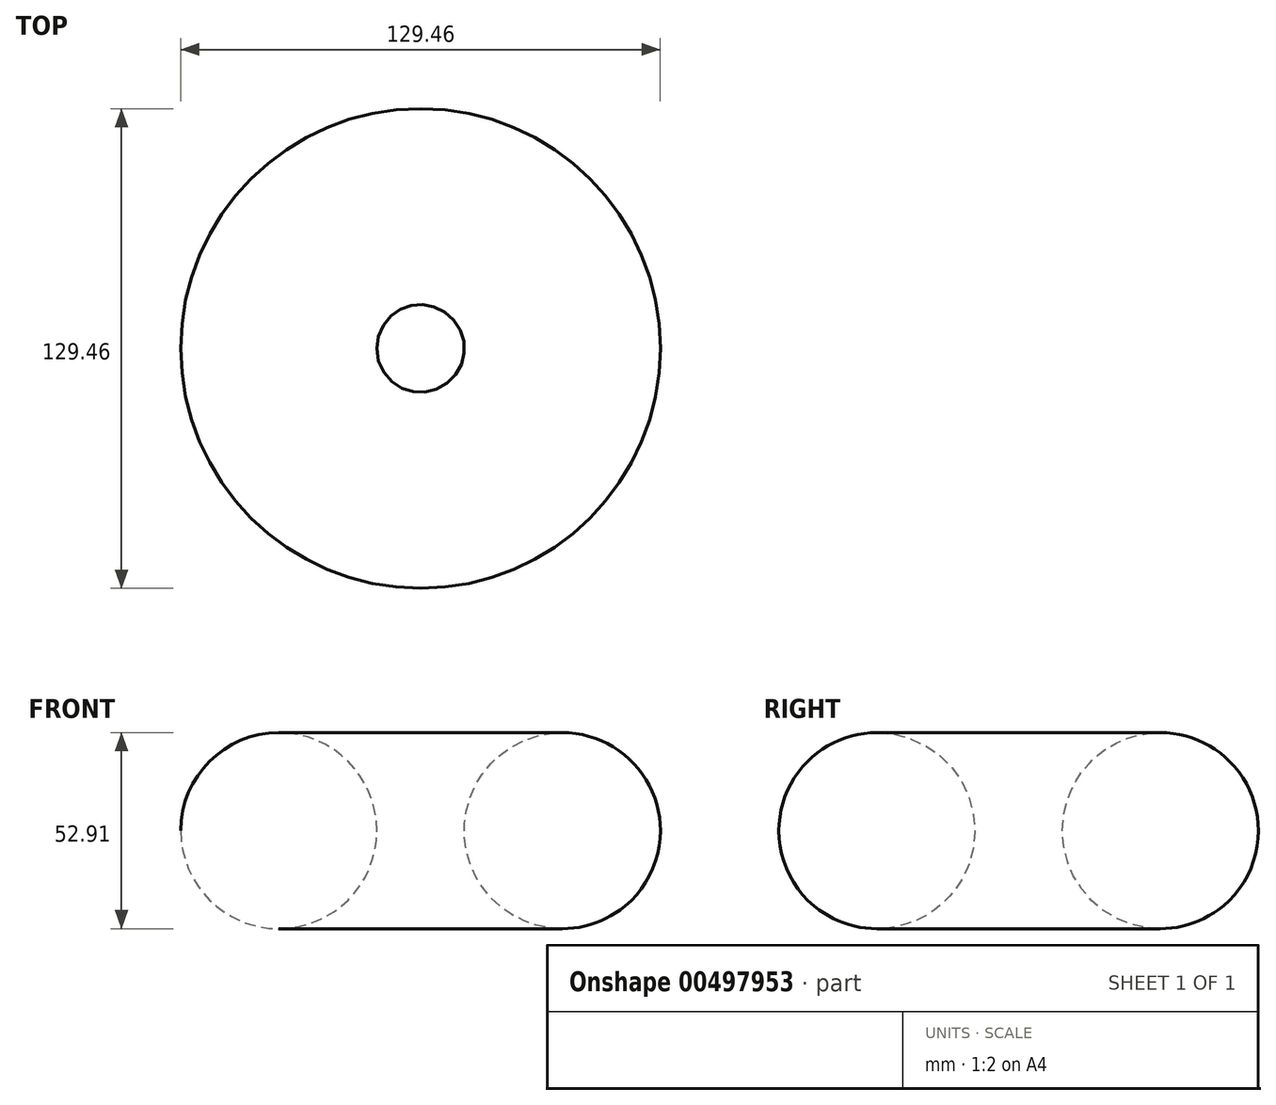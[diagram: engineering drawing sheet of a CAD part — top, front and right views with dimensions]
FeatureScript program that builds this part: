
annotation { "Feature Type Name" : "Feature", "Feature Type Description" : "" }
export const myFeature = defineFeature(function(context is Context, id is Id, definition is map)
    precondition{}
    {
        {
            var Q0;
            Q0=qCreatedBy(makeId("Front.planeOp"),FACE);
            var sketch = newSketch(context, id + "F0", { "sketchPlane" : qUnion([Q0])});
            skLineSegment(sketch, "E0", {"start": v(0, 0) * mm, "end": v(0, 46.05) * mm, "construction": true});
            skCircle(sketch, "E1", {"center": v(38.28, 35.11) * mm, "radius": 26.46 * mm});
            skSolve(sketch);
        }
        {
            var Q0;
            Q0=makeQuery(id+"F0.imprint","IMPRINT",FACE,{"disambiguationData":[TD([[makeQuery(id+"F0.imprint","IMPRINT",EDGE,{"derivedFrom":sQuery(id+"F0.wireOp",EDGE,"E1")}),1.0]])]});
            var Q1;
            Q1=sQuery(id+"F0.wireOp",EDGE,"E0");
            revolve(context, id + "F1", {"entities" : qUnion([Q0]), "axis" : qUnion([Q1]), "revolveType" : RevolveType.FULL});
        }
    });
